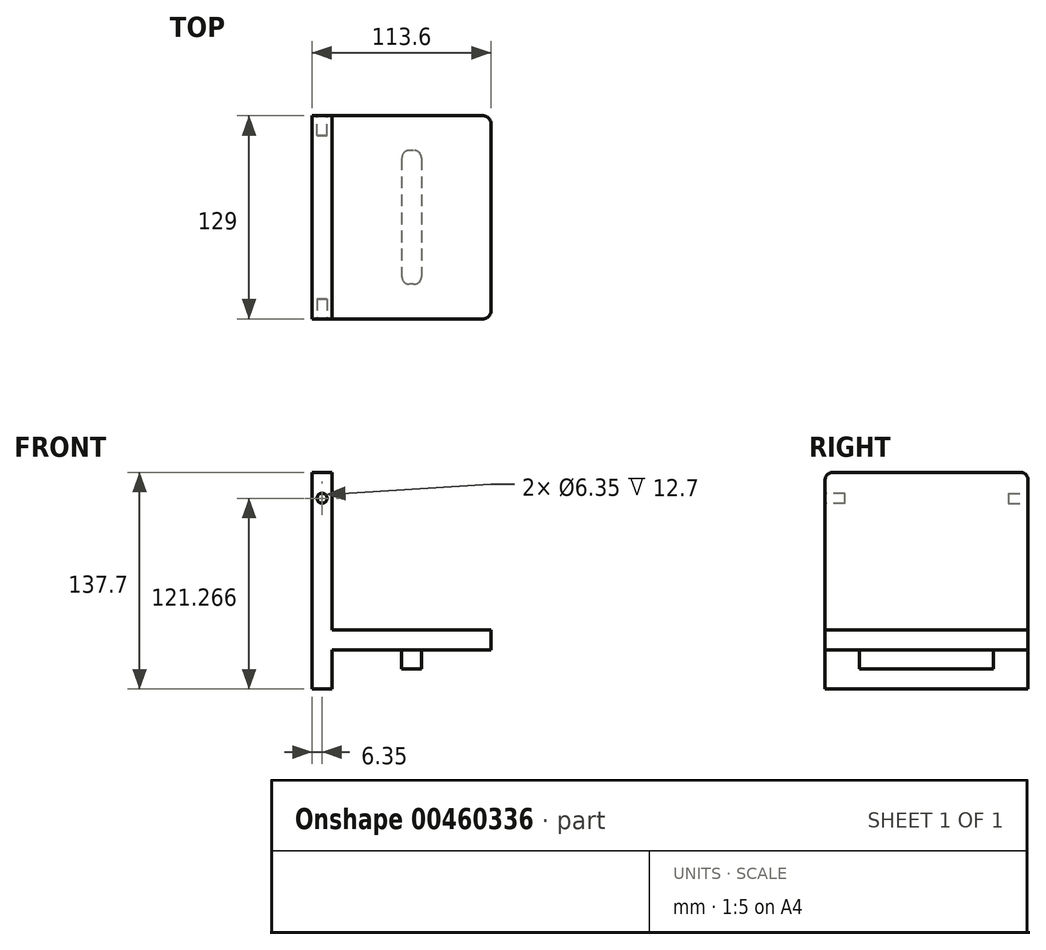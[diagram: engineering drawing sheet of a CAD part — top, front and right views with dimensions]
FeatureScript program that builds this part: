
annotation { "Feature Type Name" : "Feature", "Feature Type Description" : "" }
export const myFeature = defineFeature(function(context is Context, id is Id, definition is map)
    precondition{}
    {
        {
            var Q0;
            Q0=qCreatedBy(makeId("Top.planeOp"),FACE);
            var sketch = newSketch(context, id + "F0", { "sketchPlane" : qUnion([Q0])});
            skLineSegment(sketch, "E0.bottom", {"start": v(56.8, -64.5) * mm, "end": v(-56.8, -64.5) * mm});
            skLineSegment(sketch, "E0.top", {"start": v(56.8, 64.5) * mm, "end": v(-56.8, 64.5) * mm});
            skLineSegment(sketch, "E0.left", {"start": v(56.8, -64.5) * mm, "end": v(56.8, 64.5) * mm});
            skLineSegment(sketch, "E0.right", {"start": v(-56.8, -64.5) * mm, "end": v(-56.8, 64.5) * mm});
            skPoint(sketch, "E0.middle", {"position": v(0, 0) * mm});
            skSolve(sketch);
        }
        {
            var Q0;
            Q0=qSketchRegion(id+"F0",true);
            extrude(context, id + "F1", {"entities" : qUnion([Q0]), "depth" : 12.7 * mm});
        }
        {
            var Q0;
            Q0=makeQuery(id+"F1.opExtrude","CAP_FACE",FACE,{"disambiguationData":[OSD([sQuery(id+"F0.wireOp",EDGE,"E0.bottom"),sQuery(id+"F0.wireOp",EDGE,"E0.top"),sQuery(id+"F0.wireOp",EDGE,"E0.left"),sQuery(id+"F0.wireOp",EDGE,"E0.right")])],"isStart":false});
            var sketch = newSketch(context, id + "F2", { "sketchPlane" : qUnion([Q0])});
            skLineSegment(sketch, "E1.bottom", {"start": v(-56.8, 64.5) * mm, "end": v(-44.1, 64.5) * mm});
            skLineSegment(sketch, "E1.top", {"start": v(-56.8, -64.5) * mm, "end": v(-44.1, -64.5) * mm});
            skLineSegment(sketch, "E1.left", {"start": v(-56.8, 64.5) * mm, "end": v(-56.8, -64.5) * mm});
            skLineSegment(sketch, "E1.right", {"start": v(-44.1, 64.5) * mm, "end": v(-44.1, -64.5) * mm});
            skSolve(sketch);
        }
        {
            var Q0;
            Q0=qSketchRegion(id+"F2",true);
            extrude(context, id + "F3", {"entities" : qUnion([Q0]), "operationType" : NewBodyOperationType.ADD, "depth" : 100 * mm});
        }
        {
            var Q0;
            Q0=makeQuery(id+"F3.boolean.opBoolean","MERGE",FACE,{"derivedFrom":[makeQuery(id+"F1.opExtrude","SWEPT_FACE",FACE,{"disambiguationData":[OSD([sQuery(id+"F0.wireOp",EDGE,"E0.bottom")])]}),makeQuery(id+"F3.opExtrude","SWEPT_FACE",FACE,{"disambiguationData":[OSD([sQuery(id+"F2.wireOp",EDGE,"E1.top")])]})]});
            var sketch = newSketch(context, id + "F4", { "sketchPlane" : qUnion([Q0])});
            skCircle(sketch, "E2", {"center": v(-50.45, 96.27) * mm, "radius": 3.17 * mm});
            skSolve(sketch);
        }
        {
            var Q0;
            Q0=makeQuery(id+"F4.imprint","IMPRINT",FACE,{"disambiguationData":[TD([[makeQuery(id+"F4.imprint","IMPRINT",EDGE,{"derivedFrom":sQuery(id+"F4.wireOp",EDGE,"E2")}),1.0]])]});
            extrude(context, id + "F5", {"entities" : qUnion([Q0]), "operationType" : NewBodyOperationType.REMOVE, "oppositeDirection" : true, "depth" : 12.7 * mm});
        }
        {
            var Q0;
            Q0=makeQuery(id+"F3.opExtrude","CAP_EDGE",EDGE,{"disambiguationData":[OSD([sQuery(id+"F2.wireOp",EDGE,"E1.top")])],"isStart":false});
            var Q1;
            Q1=makeQuery(id+"F3.opExtrude","CAP_EDGE",EDGE,{"disambiguationData":[OSD([sQuery(id+"F2.wireOp",EDGE,"E1.bottom")])],"isStart":false});
            var Q2;
            Q2=makeQuery(id+"F1.opExtrude","SWEPT_EDGE",EDGE,{"disambiguationData":[OSD([sQuery(id+"F0.wireOp",EDGE,"E0.bottom"),sQuery(id+"F0.wireOp",EDGE,"E0.left")])]});
            var Q3;
            Q3=makeQuery(id+"F1.opExtrude","SWEPT_EDGE",EDGE,{"disambiguationData":[OSD([sQuery(id+"F0.wireOp",EDGE,"E0.top"),sQuery(id+"F0.wireOp",EDGE,"E0.left")])]});
            fillet(context, id + "F6", {"entities" : qUnion([Q0, Q1, Q2, Q3]), "radius" : 5 * mm, "tangentPropagation" : true, "allowEdgeOverflow" : false});
        }
        {
            var Q0;
            Q0=makeQuery(id+"F1.opExtrude","CAP_FACE",FACE,{"disambiguationData":[OSD([sQuery(id+"F0.wireOp",EDGE,"E0.bottom"),sQuery(id+"F0.wireOp",EDGE,"E0.top"),sQuery(id+"F0.wireOp",EDGE,"E0.left"),sQuery(id+"F0.wireOp",EDGE,"E0.right")])],"isStart":true});
            var sketch = newSketch(context, id + "F7", { "sketchPlane" : qUnion([Q0])});
            skLineSegment(sketch, "E3.bottom", {"start": v(-56.8, 64.5) * mm, "end": v(-44.1, 64.5) * mm});
            skLineSegment(sketch, "E3.top", {"start": v(-56.8, -64.5) * mm, "end": v(-44.1, -64.5) * mm});
            skLineSegment(sketch, "E3.left", {"start": v(-56.8, 64.5) * mm, "end": v(-56.8, -64.5) * mm});
            skLineSegment(sketch, "E3.right", {"start": v(-44.1, 64.5) * mm, "end": v(-44.1, -64.5) * mm});
            skSolve(sketch);
        }
        {
            var Q0;
            Q0=qSketchRegion(id+"F7",true);
            extrude(context, id + "F8", {"entities" : qUnion([Q0]), "operationType" : NewBodyOperationType.ADD, "depth" : 25 * mm});
        }
        {
            var Q0;
            Q0=makeQuery(id+"F1.opExtrude","CAP_FACE",FACE,{"disambiguationData":[OSD([sQuery(id+"F0.wireOp",EDGE,"E0.bottom"),sQuery(id+"F0.wireOp",EDGE,"E0.top"),sQuery(id+"F0.wireOp",EDGE,"E0.left"),sQuery(id+"F0.wireOp",EDGE,"E0.right")])],"isStart":true});
            var sketch = newSketch(context, id + "F9", { "sketchPlane" : qUnion([Q0])});
            skLineSegment(sketch, "E4.bottom", {"start": v(12.75, -42.53) * mm, "end": v(0.15, -42.53) * mm});
            skLineSegment(sketch, "E4.top", {"start": v(12.75, 42.53) * mm, "end": v(0.15, 42.53) * mm});
            skLineSegment(sketch, "E4.left", {"start": v(12.75, -42.53) * mm, "end": v(12.75, 42.53) * mm});
            skLineSegment(sketch, "E4.right", {"start": v(0.15, -42.53) * mm, "end": v(0.15, 42.53) * mm});
            skPoint(sketch, "E4.middle", {"position": v(6.45, 0) * mm});
            skSolve(sketch);
        }
        {
            var Q0;
            Q0=qSketchRegion(id+"F9",true);
            extrude(context, id + "F10", {"entities" : qUnion([Q0]), "operationType" : NewBodyOperationType.ADD, "depth" : 12 * mm});
        }
        {
            var Q0;
            Q0=makeQuery(id+"F10.opExtrude","SWEPT_EDGE",EDGE,{"disambiguationData":[OSD([sQuery(id+"F9.wireOp",EDGE,"E4.top"),sQuery(id+"F9.wireOp",EDGE,"E4.right")])]});
            var Q1;
            Q1=makeQuery(id+"F10.opExtrude","SWEPT_EDGE",EDGE,{"disambiguationData":[OSD([sQuery(id+"F9.wireOp",EDGE,"E4.top"),sQuery(id+"F9.wireOp",EDGE,"E4.left")])]});
            var Q2;
            Q2=makeQuery(id+"F10.opExtrude","SWEPT_EDGE",EDGE,{"disambiguationData":[OSD([sQuery(id+"F9.wireOp",EDGE,"E4.bottom"),sQuery(id+"F9.wireOp",EDGE,"E4.right")])]});
            var Q3;
            Q3=makeQuery(id+"F10.opExtrude","SWEPT_EDGE",EDGE,{"disambiguationData":[OSD([sQuery(id+"F9.wireOp",EDGE,"E4.bottom"),sQuery(id+"F9.wireOp",EDGE,"E4.left")])]});
            fillet(context, id + "F11", {"entities" : qUnion([Q0, Q1, Q2, Q3]), "radius" : 5 * mm, "tangentPropagation" : true, "allowEdgeOverflow" : false});
        }
        {
            var Q0;
            Q0=makeQuery(id+"F8.boolean.opBoolean","MERGE",FACE,{"derivedFrom":[makeQuery(id+"F3.boolean.opBoolean","MERGE",FACE,{"derivedFrom":[makeQuery(id+"F1.opExtrude","SWEPT_FACE",FACE,{"disambiguationData":[OSD([sQuery(id+"F0.wireOp",EDGE,"E0.top")])]}),makeQuery(id+"F3.opExtrude","SWEPT_FACE",FACE,{"disambiguationData":[OSD([sQuery(id+"F2.wireOp",EDGE,"E1.bottom")])]})]}),makeQuery(id+"F8.opExtrude","SWEPT_FACE",FACE,{"disambiguationData":[OSD([sQuery(id+"F7.wireOp",EDGE,"E3.top")])]})]});
            var sketch = newSketch(context, id + "F12", { "sketchPlane" : qUnion([Q0])});
            skCircle(sketch, "E5", {"center": v(50.45, 96.27) * mm, "radius": 3.17 * mm});
            skSolve(sketch);
        }
        {
            var Q0;
            Q0=qSketchRegion(id+"F12",true);
            extrude(context, id + "F13", {"entities" : qUnion([Q0]), "operationType" : NewBodyOperationType.REMOVE, "oppositeDirection" : true, "depth" : 12.7 * mm});
        }
    });
